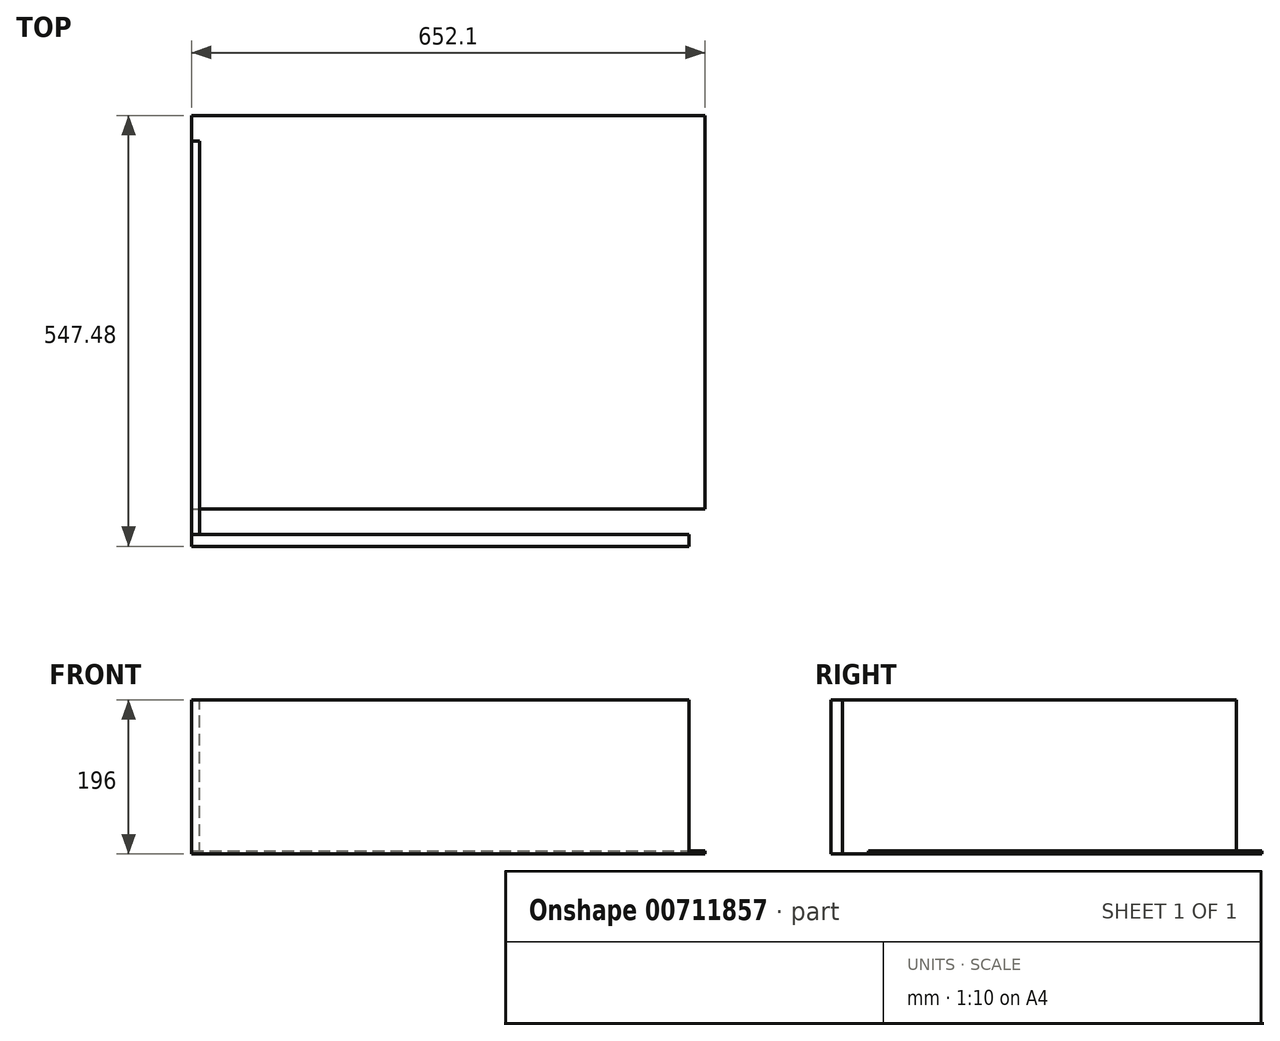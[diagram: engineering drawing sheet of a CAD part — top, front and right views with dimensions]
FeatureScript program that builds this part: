
annotation { "Feature Type Name" : "Feature", "Feature Type Description" : "" }
export const myFeature = defineFeature(function(context is Context, id is Id, definition is map)
    precondition{}
    {
        {
            var Q0;
            Q0=qCreatedBy(makeId("Front.planeOp"),FACE);
            var sketch = newSketch(context, id + "F0", { "sketchPlane" : qUnion([Q0])});
            skLineSegment(sketch, "E0.bottom", {"start": v(0, 0) * mm, "end": v(632.1, 0) * mm});
            skLineSegment(sketch, "E0.top", {"start": v(0, 196) * mm, "end": v(632.1, 196) * mm});
            skLineSegment(sketch, "E0.left", {"start": v(0, 0) * mm, "end": v(0, 196) * mm});
            skLineSegment(sketch, "E0.right", {"start": v(632.1, 0) * mm, "end": v(632.1, 196) * mm});
            skSolve(sketch);
        }
        {
            var Q0;
            Q0=qSketchRegion(id+"F0",true);
            extrude(context, id + "F1", {"entities" : qUnion([Q0]), "depth" : 15 * mm, "offsetDistance" : 25 * mm});
        }
        {
            var Q0;
            Q0=qCreatedBy(makeId("Top.planeOp"),FACE);
            var sketch = newSketch(context, id + "F2", { "sketchPlane" : qUnion([Q0])});
            skLineSegment(sketch, "E1.bottom", {"start": v(0, 32.48) * mm, "end": v(652.1, 32.48) * mm});
            skLineSegment(sketch, "E1.top", {"start": v(0, 532.48) * mm, "end": v(652.1, 532.48) * mm});
            skLineSegment(sketch, "E1.left", {"start": v(0, 32.48) * mm, "end": v(0, 532.48) * mm});
            skLineSegment(sketch, "E1.right", {"start": v(652.1, 32.48) * mm, "end": v(652.1, 532.48) * mm});
            skSolve(sketch);
        }
        {
            var Q0;
            Q0=qSketchRegion(id+"F2",true);
            extrude(context, id + "F3", {"entities" : qUnion([Q0]), "depth" : 4 * mm, "offsetDistance" : 25 * mm});
        }
        {
            var Q0;
            Q0=qCreatedBy(makeId("Right.planeOp"),FACE);
            var sketch = newSketch(context, id + "F4", { "sketchPlane" : qUnion([Q0])});
            skLineSegment(sketch, "E2.bottom", {"start": v(0, 0) * mm, "end": v(500, 0) * mm});
            skLineSegment(sketch, "E2.top", {"start": v(0, 196) * mm, "end": v(500, 196) * mm});
            skLineSegment(sketch, "E2.left", {"start": v(0, 0) * mm, "end": v(0, 196) * mm});
            skLineSegment(sketch, "E2.right", {"start": v(500, 0) * mm, "end": v(500, 196) * mm});
            skSolve(sketch);
        }
        {
            var Q0;
            Q0=qSketchRegion(id+"F4",true);
            extrude(context, id + "F5", {"entities" : qUnion([Q0]), "depth" : 10 * mm, "offsetDistance" : 25 * mm});
        }
    });
